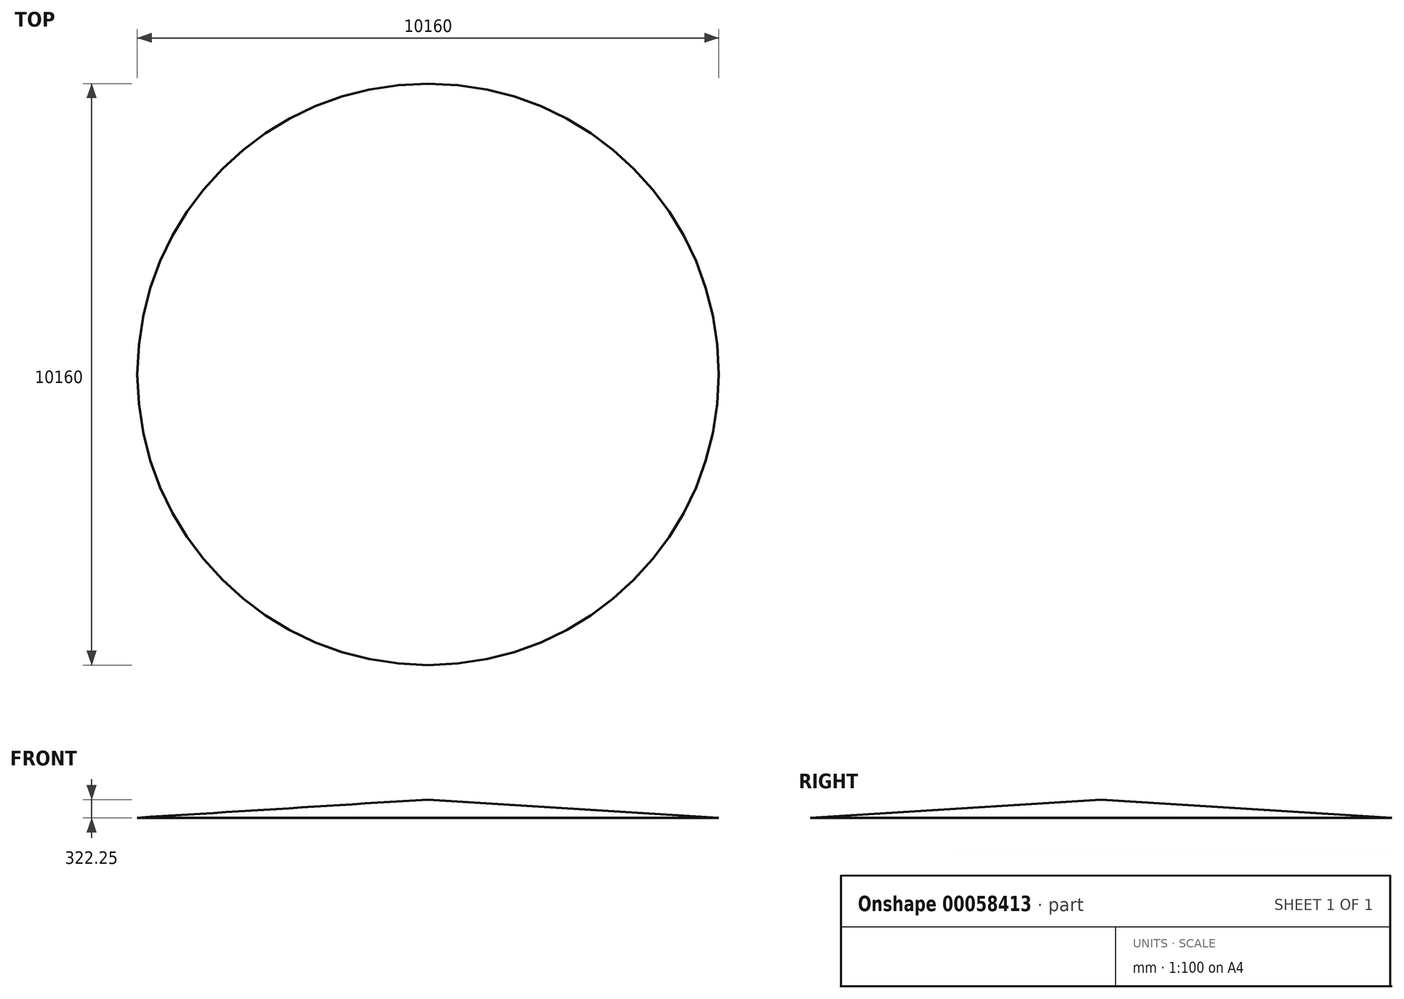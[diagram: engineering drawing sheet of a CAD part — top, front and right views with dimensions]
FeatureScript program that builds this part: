
annotation { "Feature Type Name" : "Feature", "Feature Type Description" : "" }
export const myFeature = defineFeature(function(context is Context, id is Id, definition is map)
    precondition{}
    {
        {
            var Q0;
            Q0=qCreatedBy(makeId("Front.planeOp"),FACE);
            var sketch = newSketch(context, id + "F0", { "sketchPlane" : qUnion([Q0])});
            skLineSegment(sketch, "E0", {"start": v(0, 0) * mm, "end": v(5029.2, 0) * mm});
            skLineSegment(sketch, "E1", {"start": v(5029.2, 0) * mm, "end": v(0, 314.3) * mm});
            skLineSegment(sketch, "E2", {"start": v(0, 314.3) * mm, "end": v(0, 0) * mm});
            skLineSegment(sketch, "E3", {"start": v(4952.85, 0) * mm, "end": v(0, 309.53) * mm});
            skLineSegment(sketch, "E4", {"start": v(5029.2, 0) * mm, "end": v(5080, -3.17) * mm});
            skLineSegment(sketch, "E5", {"start": v(5080, -3.17) * mm, "end": v(5080, -15.87) * mm});
            skLineSegment(sketch, "E6", {"start": v(4952.85, 0) * mm, "end": v(5080, -7.95) * mm});
            skPoint(sketch, "E6.endSnap0", {"position": v(5080, -9.52) * mm});
            skLineSegment(sketch, "E7", {"start": v(5080, -7.95) * mm, "end": v(5032.6, -4.98) * mm});
            skSolve(sketch);
        }
        {
            var Q0;
            {var subQ0=sQuery(id+"F0.wireOp",EDGE,"E1");Q0=makeQuery(id+"F0.imprint","IMPRINT",FACE,{"disambiguationData":[TD([[makeQuery(id+"F0.imprint","IMPRINT",EDGE,{"derivedFrom":subQ0}),1.0]])]});}
            var Q1;
            {var subQ1=sQuery(id+"F0.wireOp",EDGE,"E4");Q1=makeQuery(id+"F0.imprint","IMPRINT",FACE,{"disambiguationData":[TD([[makeQuery(id+"F0.imprint","IMPRINT",EDGE,{"derivedFrom":subQ1}),-1.0]])]});}
            var Q2;
            Q2=sQuery(id+"F0.wireOp",EDGE,"E2");
            revolve(context, id + "F1", {"entities" : qUnion([Q0, Q1]), "axis" : qUnion([Q2]), "revolveType" : RevolveType.FULL});
        }
    });
